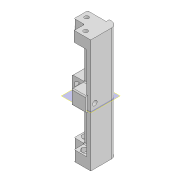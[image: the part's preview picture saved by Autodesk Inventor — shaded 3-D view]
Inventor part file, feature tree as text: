
AUTODESK INVENTOR PART (.ipt)
format: ipt  version: 2020 (Build 240168000, 168)  size: 354,816 bytes
history: native  units: mm
features: extrude x13, sketch x13, other x7, fillet x2
ambient origin geometry x8: Origin, YZ Plane, XZ Plane, XY Plane, X Axis, Y Axis, Z Axis, Center Point
bodies: Body1 (feature_tree)
feature tree (35):
  other  "Sólido1"
  extrude  "Extrusão1"  Depth=16.0mm
  extrude  "Extrusão2"  Depth=3.0mm
  extrude  "Extrusão3"  Depth=3.0mm
  extrude  "Extrusão4"  Depth=6.0mm
  extrude  "Extrusão5"  Depth=8.0mm
  fillet  "Arredondamento1"  Radius=110.0mm
  extrude  "Extrusão6"  Depth=10.0mm
  extrude  "Extrusão7"  TaperAngle=0.0deg  [1 undecoded]
  other  "Plano de trabalho1"
  extrude  "Extrusão9"  Depth=5.0mm
  extrude  "Extrusão10"  Depth=10.0mm
  extrude  "Extrusão11"  Depth=4.0mm
  extrude  "Extrusão12"  Depth=5.0mm
  extrude  "Extrusão13"  Depth=1.0mm TaperAngle=0.0deg
  fillet  "Arredondamento2"  Radius=1.0mm
  extrude  "Extrusão14"  Depth=6.95mm
  sketch  "Esboço1"  dims[d0=16.0mm d1=16.0mm]
  sketch  "Esboço2"  dims[d2=8.0mm d3=3.0mm]
  sketch  "Esboço3"  dims[d4=8.0mm d5=3.0mm]
  sketch  "Esboço4"  dims[d6=6.0mm d7=5.2mm]
  sketch  "Esboço5"  dims[d8=8.0mm d9=8.0mm d10=110.0mm d11=0.0mm]
  sketch  "Esboço6"  dims[d12=10.0mm d13=10.0mm]
  sketch  "Esboço7"  dims[d14=10.0mm d15=0.0mm d16=0.0mm]
  other  "Contorno projetado1"
  other  "Contorno projetado2"
  sketch  "Esboço9"  dims[d17=4.0mm d18=5.0mm]
  other  "Contorno projetado3"
  other  "Contorno projetado4"
  sketch  "Esboço10"  dims[d19=200.0mm d20=0.0mm d21=10.0mm]
  sketch  "Esboço11"  dims[d22=10.0mm d23=0.0mm d24=4.0mm]
  sketch  "Esboço12"  dims[d25=5.0mm d26=7.0mm]
  sketch  "Esboço13"  dims[d27=6.0mm d28=200.0mm d29=0.0mm d30=1.0mm]
  sketch  "Esboço14"  dims[d31=13.0mm d32=6.95mm d33=6.95mm d34=4.0mm d35=0.0mm d36=4.0mm d37=0.0mm d38=0.0mm d44=0.0mm d45=-50.0mm d46=12.0mm d47=12.0mm d48=2.0mm d49=0.0mm d50=12.0mm d51=0.0mm d52=4.5mm d53=6.0mm d54=20.0mm d55=0.0mm d56=4.5mm d57=6.0mm d58=20.0mm d59=0.0mm d60=6.95mm d61=4.0mm d62=0.0mm d63=6.95mm d64=4.0mm d65=0.0mm d66=1.0mm d67=3.0mm d68=0.0mm d69=1.0mm d70=0.0mm]
  other  "Contorno projetado5"
note: 1 required parameter value undecoded (feature->parameter linkage not recoverable at this tier; creation-order binding heuristic only, values carry confidence <= 0.55)
